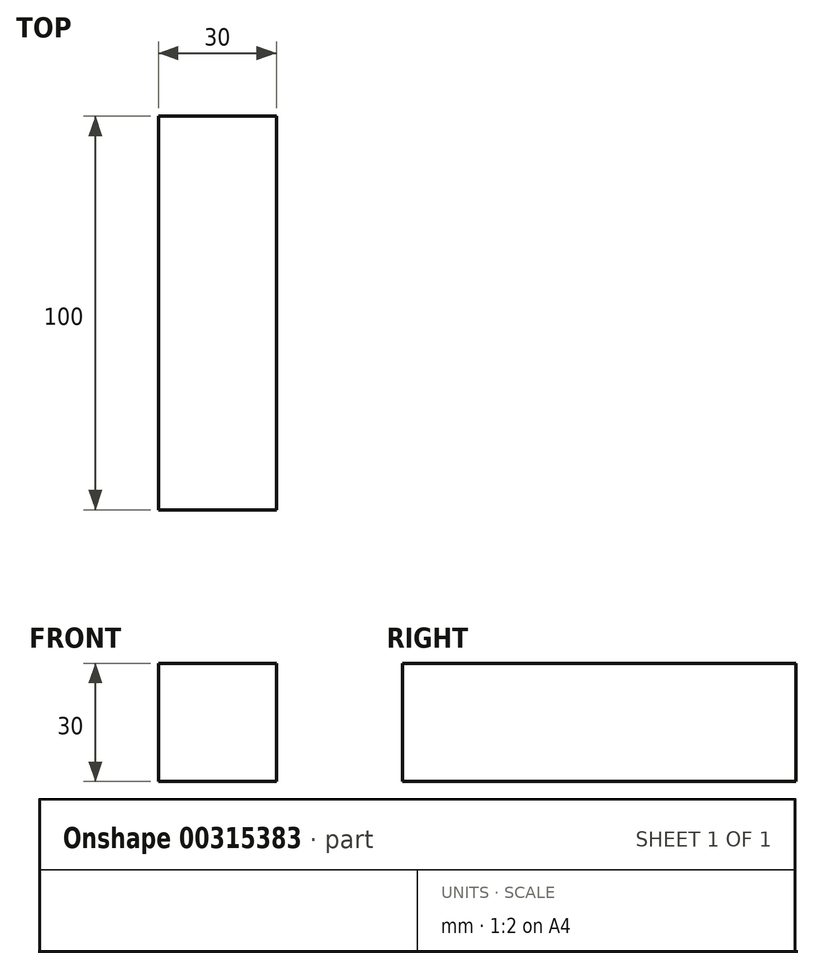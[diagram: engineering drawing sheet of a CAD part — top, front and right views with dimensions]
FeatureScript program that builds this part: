
annotation { "Feature Type Name" : "Feature", "Feature Type Description" : "" }
export const myFeature = defineFeature(function(context is Context, id is Id, definition is map)
    precondition{}
    {
        {
            var Q0;
            Q0=qCreatedBy(makeId("Top.planeOp"),FACE);
            var sketch = newSketch(context, id + "F0", { "sketchPlane" : qUnion([Q0])});
            skLineSegment(sketch, "E0.bottom", {"start": v(15, 50) * mm, "end": v(-15, 50) * mm});
            skLineSegment(sketch, "E0.top", {"start": v(15, -50) * mm, "end": v(-15, -50) * mm});
            skLineSegment(sketch, "E0.left", {"start": v(15, 50) * mm, "end": v(15, -50) * mm});
            skLineSegment(sketch, "E0.right", {"start": v(-15, 50) * mm, "end": v(-15, -50) * mm});
            skPoint(sketch, "E0.middle", {"position": v(0, 0) * mm});
            skSolve(sketch);
        }
        {
            var Q0;
            Q0=makeQuery(id+"F0.imprint","IMPRINT",FACE,{"disambiguationData":[TD([[makeQuery(id+"F0.imprint","IMPRINT",EDGE,{"derivedFrom":sQuery(id+"F0.wireOp",EDGE,"E0.bottom")}),1.0]])]});
            extrude(context, id + "F1", {"entities" : qUnion([Q0]), "depth" : 30 * mm});
        }
    });
